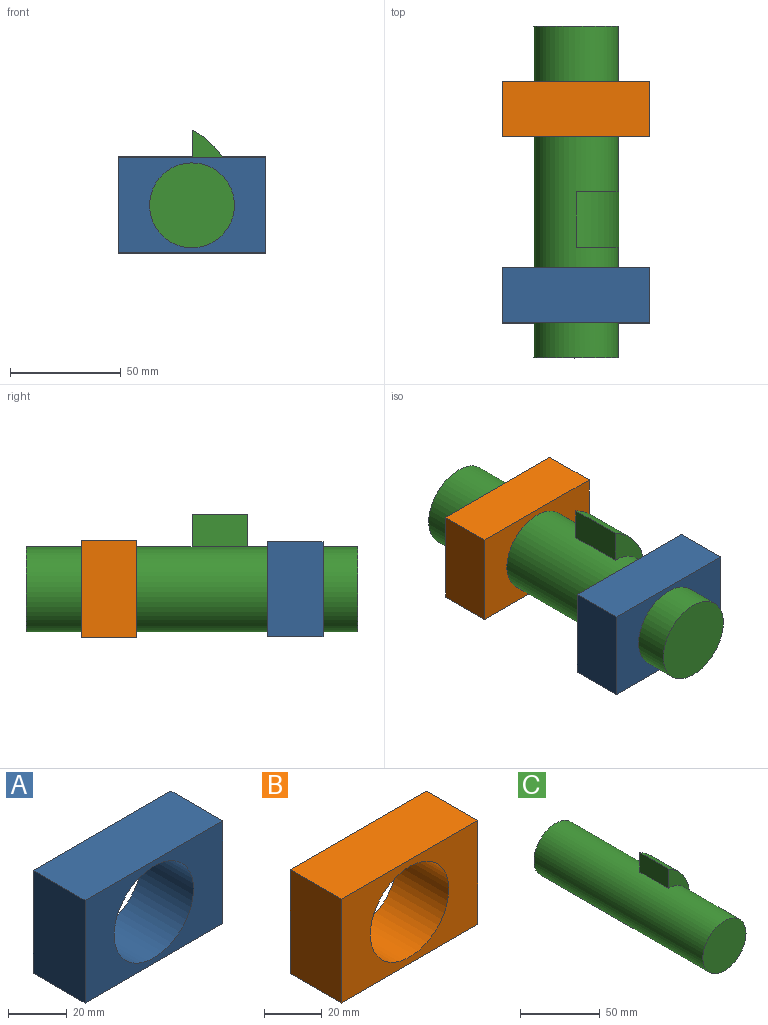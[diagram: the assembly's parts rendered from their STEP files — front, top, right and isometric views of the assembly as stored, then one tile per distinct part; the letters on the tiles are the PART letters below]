
ASSEMBLY  parts=3 mates=2
PART A: 7 faces, bbox 66.5x25x42.9 mm
  f0: plane 42.95x25mm, normal (-1,0,0), area 1073.6mm2, adj f1,f4,f5,f6
  f1: plane 66.51x25mm, normal (0,0,-1), area 1662.8mm2, adj f0,f2,f5,f6
  f2: plane 42.95x25mm, normal (1,0,0), area 1073.6mm2, adj f1,f4,f5,f6
  f3: cylinder r=19.18mm len=38.36mm, axis (0,1,0), area 3012.6mm2, adj f5,f6
  f4: plane 66.51x25mm, normal (0,0,1), area 1662.8mm2, adj f0,f2,f5,f6
  f5: plane 66.51x42.95mm, normal (0,-1,0), area 1700.9mm2, adj f0,f1,f2,f3,f4
  f6: plane 66.51x42.95mm, normal (0,1,0), area 1700.9mm2, adj f0,f1,f2,f3,f4
PART B: 7 faces, bbox 66.7x25x44 mm
  f0: plane 43.98x25mm, normal (1,0,0), area 1099.5mm2, adj f1,f4,f5,f6
  f1: plane 66.66x25mm, normal (0,0,-1), area 1666.6mm2, adj f0,f2,f5,f6
  f2: plane 43.98x25mm, normal (-1,0,0), area 1099.5mm2, adj f1,f4,f5,f6
  f3: cylinder r=19.18mm len=38.36mm, axis (0,-1,0), area 3012.6mm2, adj f5,f6
  f4: plane 66.66x25mm, normal (0,0,1), area 1666.6mm2, adj f0,f2,f5,f6
  f5: plane 66.66x43.98mm, normal (0,1,0), area 1776.3mm2, adj f0,f1,f2,f3,f4
  f6: plane 66.66x43.98mm, normal (0,-1,0), area 1776.3mm2, adj f0,f1,f2,f3,f4
PART C: 7 faces, bbox 38.5x150x53.2 mm
  f0: cylinder r=19.18mm len=150mm, axis (0,1,0), area 17322.5mm2, adj f1,f2,f3,f4,f5,f6
  f1: plane 38.36x38.36mm, normal (0,-1,0), area 1155.6mm2, adj f0
  f2: plane 38.36x38.36mm, normal (0,1,0), area 1155.6mm2, adj f0
  f3: plane 34.03x19.31mm, normal (0,-1,0), area 197.5mm2, adj f0,f5,f6
  f4: plane 34.03x19.31mm, normal (0,1,0), area 197.5mm2, adj f0,f5,f6
  f5: cylinder r=34.61mm len=34.03mm, axis (0,1,0), area 1037.5mm2, adj f0,f3,f4,f6
  f6: plane 25x14.85mm, normal (-1,0,0), area 371.2mm2, adj f0,f3,f4,f5
PLACE A t=(-31.71,42.45,39.97)mm
PLACE B t=(-31.71,-48.36,39.97)mm
PLACE C t=(-31.71,1.66,39.97)mm
MATE cylindrical C.f0 <-> B.f3  axis (0,1,0) through (-31.71,1.66,39.97)mm
MATE cylindrical C.f0 <-> A.f3  axis (0,1,0) through (-31.71,1.66,39.97)mm
